# Revit family: Переходник с накидной гайкой
name_source: partatom
category: Соединительные детали трубопроводов
revit_build: Autodesk Revit 2017 (Build: 20160225_1515(x64)
units: mm (PartAtom-declared; Revit-internal decimal feet)

## family parameters
Всегда вертикально = Да
На основе рабочей плоскости = Нет
Общий = Нет
При загрузке вырезать с полостями = Нет
Размер круглого соединителя = Использовать радиус
Тип детали = Соединение

## types (10) — shared parameters
ADSK_Единица измерения = шт
ADSK_Завод-изготовитель = Sanext
URL = http://sanext.ru
Изготовитель = Sanext
Материал фитинга = DZR латунь
Разработчик = ООО ПРОРУБИМ
Разработчик (телефон) = +7(495)649-85-43
Разработчик модели (URL) = http://prorubim.com
zero-valued in all types: ADSK_Масса

## per-type parameters (varying)
| type | ADSK_Код изделия | D1 | DN | G | G/2 | G1/2 | R | R1 | S | a |
| Переходник с накидной гайкой 63xG 2 3/8" | 4378 | 85 мм | 63 мм | 80 мм | 40 мм | 42 мм | 32 мм | 29 мм | 85 мм | 80 мм |
| Переходник с накидной гайкой 50x1 3/4" | 4364 | 55 мм | 50 мм | 50 мм | 25 мм | 27 мм | 25 мм | 22 мм | 55 мм | 67 мм |
| Переходник с накидной гайкой 40 xG 2" | 4355 | 68 мм | 40 мм | 63 мм | 32 мм | 33 мм | 20 мм | 17 мм | 68 мм | 65 мм |
| Переходник с накидной гайкой 40xG 1 1/2" | 4353 | 55 мм | 40 мм | 50 мм | 25 мм | 27 мм | 20 мм | 17 мм | 55 мм | 60 мм |
| Переходник с накидной гайкой 32xG1" | 4342 | 37 мм | 32 мм | 32 мм | 16 мм | 18 мм | 16 мм | 13 мм | 37 мм | 53 мм |
| Переходник с накидной гайкой 25xG3/4" | 4331 | 30 мм | 25 мм | 25 мм | 13 мм | 14 мм | 13 мм | 10 мм | 30 мм | 45 мм |
| Переходник с накидной гайкой 20xG3/4" | 4321 | 30 мм | 20 мм | 25 мм | 13 мм | 14 мм | 10 мм | 7 мм | 30 мм | 32 мм |
| Переходник с накидной гайкой 20xG1/2" | 4320 | 25 мм | 20 мм | 20 мм | 10 мм | 12 мм | 10 мм | 7 мм | 25 мм | 40 мм |
| Переходник с накидной гайкой 16xG3/4" | 4311 | 30 мм | 16 мм | 25 мм | 13 мм | 14 мм | 8 мм | 5 мм | 30 мм | 38 мм |
| Переходник с накидной гайкой 16xG1/2" | 4310 | 25 мм | 16 мм | 20 мм | 10 мм | 12 мм | 8 мм | 5 мм | 25 мм | 32 мм |

note: column(s) folded — value = type name in every type: ADSK_Наименование
